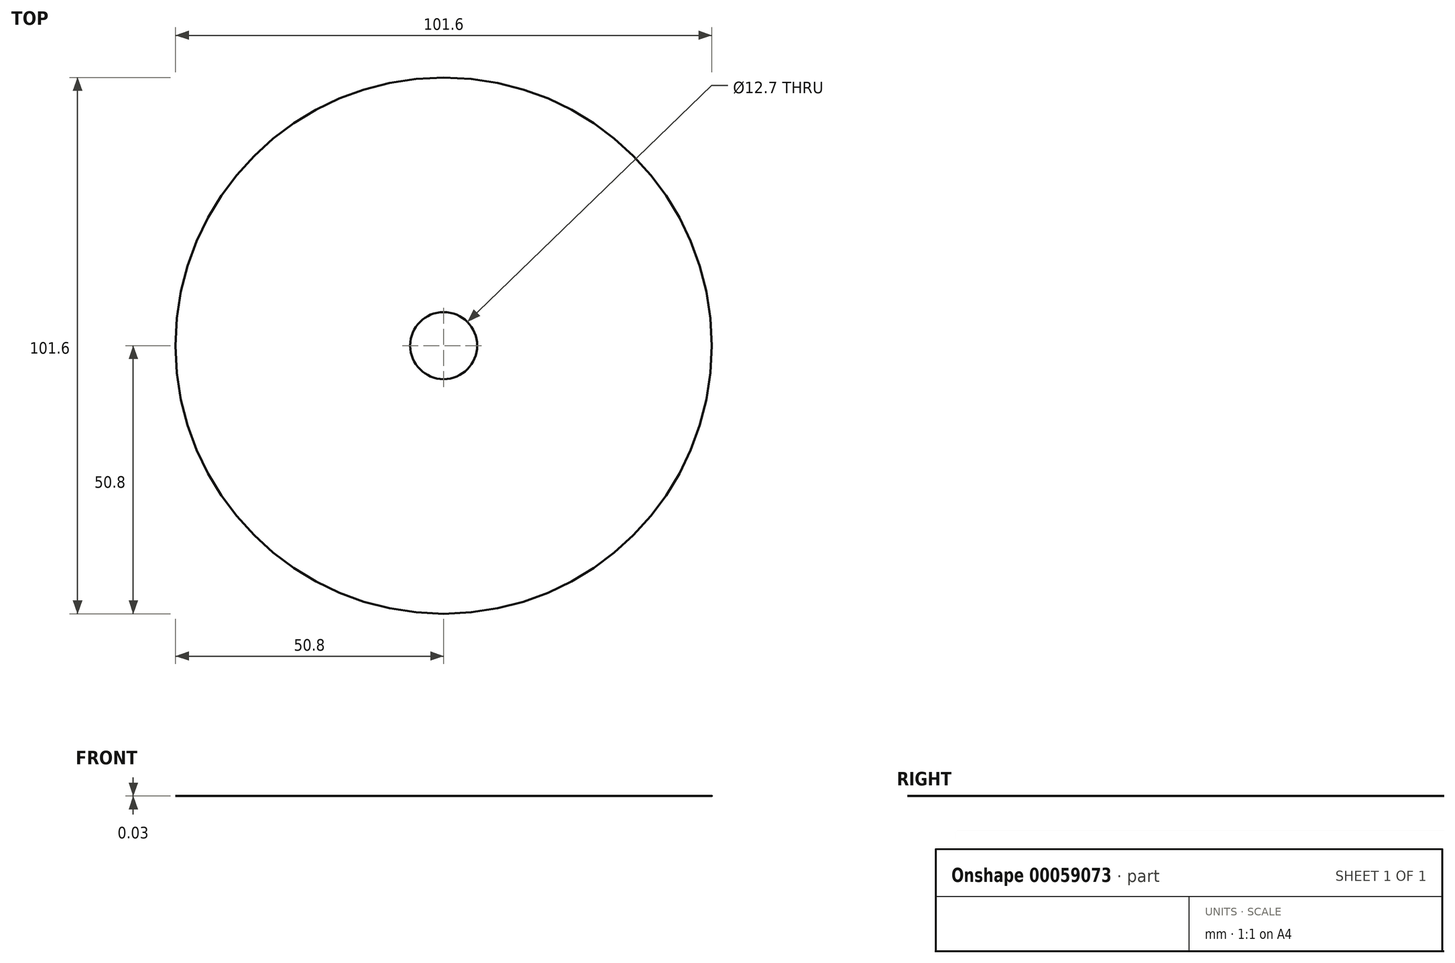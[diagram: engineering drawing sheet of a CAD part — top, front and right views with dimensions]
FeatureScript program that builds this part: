
annotation { "Feature Type Name" : "Feature", "Feature Type Description" : "" }
export const myFeature = defineFeature(function(context is Context, id is Id, definition is map)
    precondition{}
    {
        {
            var Q0;
            Q0=qCreatedBy(makeId("Top.planeOp"),FACE);
            var sketch = newSketch(context, id + "F0", { "sketchPlane" : qUnion([Q0])});
            skCircle(sketch, "E0", {"center": v(0, 0) * mm, "radius": 50.8 * mm});
            skSolve(sketch);
        }
        {
            var Q0;
            Q0=makeQuery(id+"F0.imprint","IMPRINT",FACE,{"disambiguationData":[TD([[makeQuery(id+"F0.imprint","IMPRINT",EDGE,{"derivedFrom":sQuery(id+"F0.wireOp",EDGE,"E0")}),1.0]])]});
            extrude(context, id + "F1", {"entities" : qUnion([Q0]), "depth" : 7 / 203.2 * mm});
        }
        {
            var Q0;
            Q0=makeQuery(id+"F1.opExtrude","CAP_FACE",FACE,{"disambiguationData":[OSD([sQuery(id+"F0.wireOp",EDGE,"E0")])],"isStart":false});
            var sketch = newSketch(context, id + "F2", { "sketchPlane" : qUnion([Q0])});
            skCircle(sketch, "E1", {"center": v(0, 0) * mm, "radius": 6.35 * mm});
            skSolve(sketch);
        }
        {
            var Q0;
            Q0=makeQuery(id+"F2.imprint","IMPRINT",FACE,{"disambiguationData":[TD([[makeQuery(id+"F2.imprint","IMPRINT",EDGE,{"derivedFrom":sQuery(id+"F2.wireOp",EDGE,"E1")}),1.0]])]});
            extrude(context, id + "F3", {"entities" : qUnion([Q0]), "operationType" : NewBodyOperationType.REMOVE, "oppositeDirection" : true, "depth" : 7 / 203.2 * mm});
        }
    });
